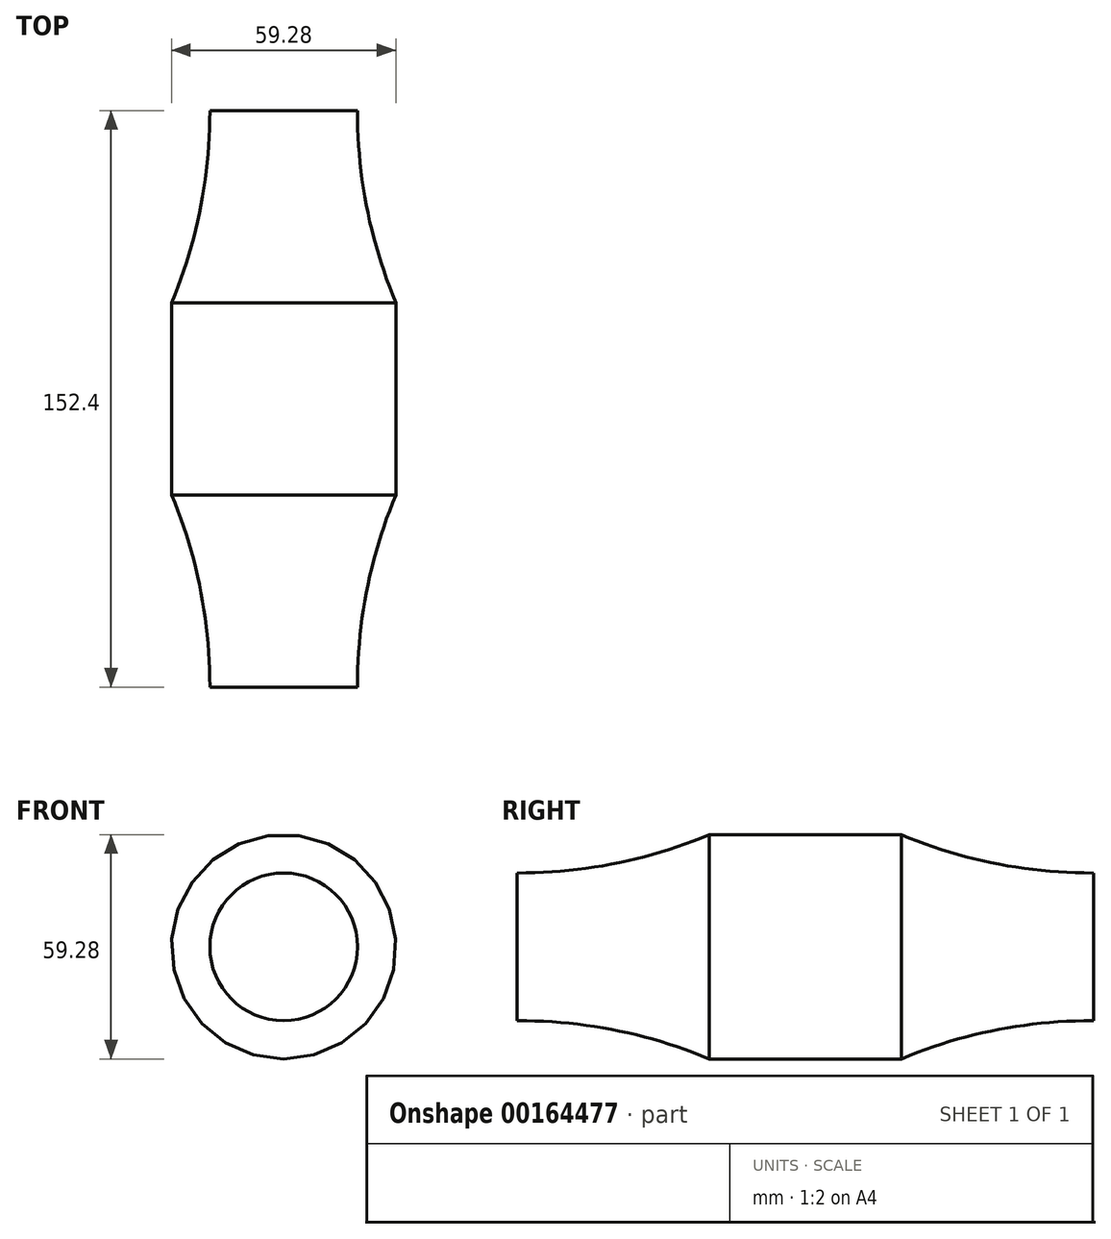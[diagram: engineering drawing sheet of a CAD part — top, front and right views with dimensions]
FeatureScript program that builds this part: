
annotation { "Feature Type Name" : "Feature", "Feature Type Description" : "" }
export const myFeature = defineFeature(function(context is Context, id is Id, definition is map)
    precondition{}
    {
        {
            var Q0;
            Q0=qCreatedBy(makeId("Front.planeOp"),FACE);
            var sketch = newSketch(context, id + "F0", { "sketchPlane" : qUnion([Q0])});
            skCircle(sketch, "E0", {"center": v(0, 0) * mm, "radius": 29.64 * mm});
            skSolve(sketch);
        }
        {
            var Q0;
            Q0=makeQuery(id+"F0.imprint","IMPRINT",FACE,{"disambiguationData":[TD([[makeQuery(id+"F0.imprint","IMPRINT",EDGE,{"derivedFrom":sQuery(id+"F0.wireOp",EDGE,"E0")}),1.0]])]});
            extrude(context, id + "F1", {"entities" : qUnion([Q0]), "depth" : 25.4 * mm});
        }
        {
            var Q0;
            Q0=qCreatedBy(makeId("Front.planeOp"),FACE);
            var sketch = newSketch(context, id + "F2", { "sketchPlane" : qUnion([Q0])});
            skCircle(sketch, "E1", {"center": v(0, 0) * mm, "radius": 19.52 * mm});
            skSolve(sketch);
        }
        {
            var Q0;
            Q0 = qSketchRegion(id + "F2", true);
            extrude(context, id + "F3", {"entities" : qUnion([Q0]), "operationType" : NewBodyOperationType.ADD, "depth" : 76.2 * mm});
        }
        {
            var Q0;
            Q0=makeQuery(id+"F3.boolean.opBoolean","INTERSECT",EDGE,{"derivedFrom":[makeQuery(id+"F1.opExtrude","CAP_FACE",FACE,{"disambiguationData":[OSD([sQuery(id+"F0.wireOp",EDGE,"E0")])],"isStart":false}),makeQuery(id+"F3.opExtrude","SWEPT_FACE",FACE,{"disambiguationData":[OSD([sQuery(id+"F2.wireOp",EDGE,"E1")])]})]});
            fillet(context, id + "F4", {"entities" : qUnion([Q0]), "radius" : 131.23 * mm, "tangentPropagation" : true, "rho" : 0.5, "crossSection" : FilletCrossSection.CONIC, "allowEdgeOverflow" : false});
        }
        {
            var Q0;
            Q0=makeQuery(id+"F1.opExtrude","SWEPT_BODY",BODY,{"disambiguationData":[OSD([sQuery(id+"F0.wireOp",EDGE,"E0")])]});
            var Q1;
            Q1=qCreatedBy(makeId("Front.planeOp"),FACE);
            mirror(context, id + "F5", {"operationType" : NewBodyOperationType.ADD, "entities" : qUnion([Q0]), "mirrorPlane" : qUnion([Q1])});
        }
    });
